# Revit family: WI2013004
name_source: partatom
category: Aparatos sanitarios
revit_build: Autodesk Revit 2016 (Build: 20150220_1215(x64)
units: mm (PartAtom-declared; Revit-internal decimal feet)

## family parameters
Anfitrión = Muro
Compartido = No
Corte con vacíos al cargar = No
Cota de conector redondo = Diámetro de uso
Número OmniClass = 23.45.00.00
Punto de cálculo de habitación = No
Siempre vertical = Sí
Tipo de pieza = Normal
Título OmniClass = Sanitary, Laundry, and Cleaning Equipment

## types (1)
- 400
    Conexión AC = No
    Conexión AF = No
    Conexión de residuos = Sí
    Conexión de ventilación = Sí
    Código de montaje = D2030
    Descripción = Set de montaje WC estanque
Con placa de accionamiento acero inoxidable
Doble descarga de 3 y 6 litros
Medidas 50 x 114
Tanque alto
Doble pulsador
Fijaciones y conector.
    Fabricante = CHC
    Imagen de tipo = WI2013004.jpg
    Modelo = WI2013004
    Pipe Material = PVC-Piping
    Structure Material = Stainless Steel, Brushed
    Tank Material = PVC, Unplasticized
    URL = www.grupochc.cl

## geometry (parser evidence)
native form markers: Sweep x2
no freeform markers — native parametric forms only
